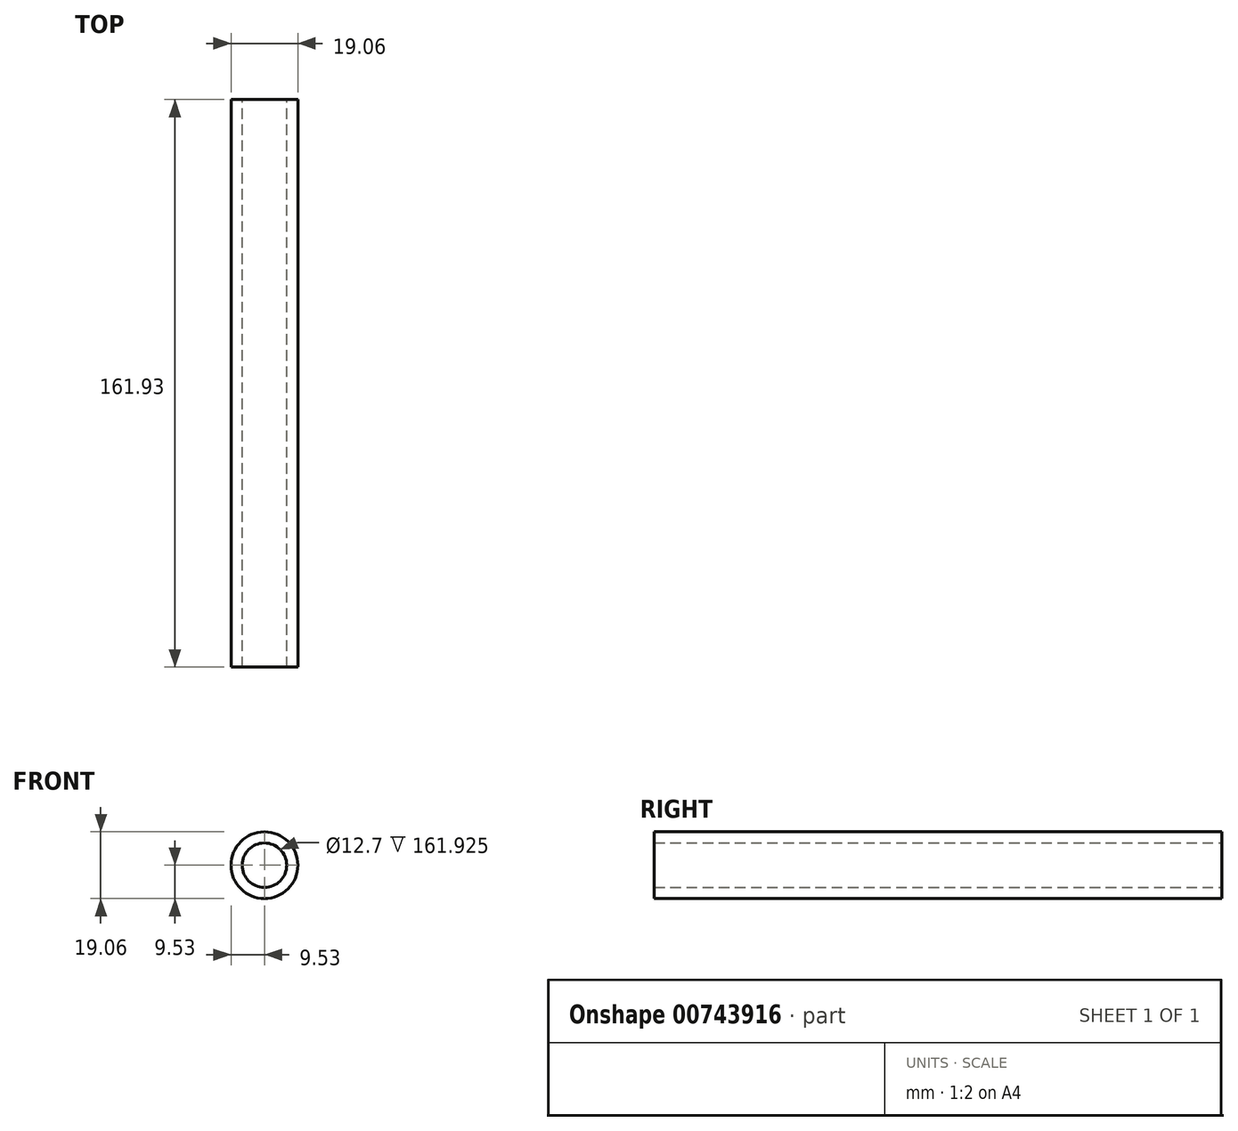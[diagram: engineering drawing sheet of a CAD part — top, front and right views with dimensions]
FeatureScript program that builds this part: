
annotation { "Feature Type Name" : "Feature", "Feature Type Description" : "" }
export const myFeature = defineFeature(function(context is Context, id is Id, definition is map)
    precondition{}
    {
        {
            var Q0;
            Q0=qCreatedBy(makeId("Front.planeOp"),FACE);
            var sketch = newSketch(context, id + "F0", { "sketchPlane" : qUnion([Q0])});
            skCircle(sketch, "E0", {"center": v(0, 0) * mm, "radius": 9.53 * mm});
            skCircle(sketch, "E1", {"center": v(0, 0) * mm, "radius": 6.35 * mm});
            skSolve(sketch);
        }
        {
            var Q0;
            Q0 = qSketchRegion(id + "F0", true);
            extrude(context, id + "F1", {"entities" : qUnion([Q0]), "depth" : 161.92 * mm, "offsetDistance" : 25.4 * mm});
        }
    });
